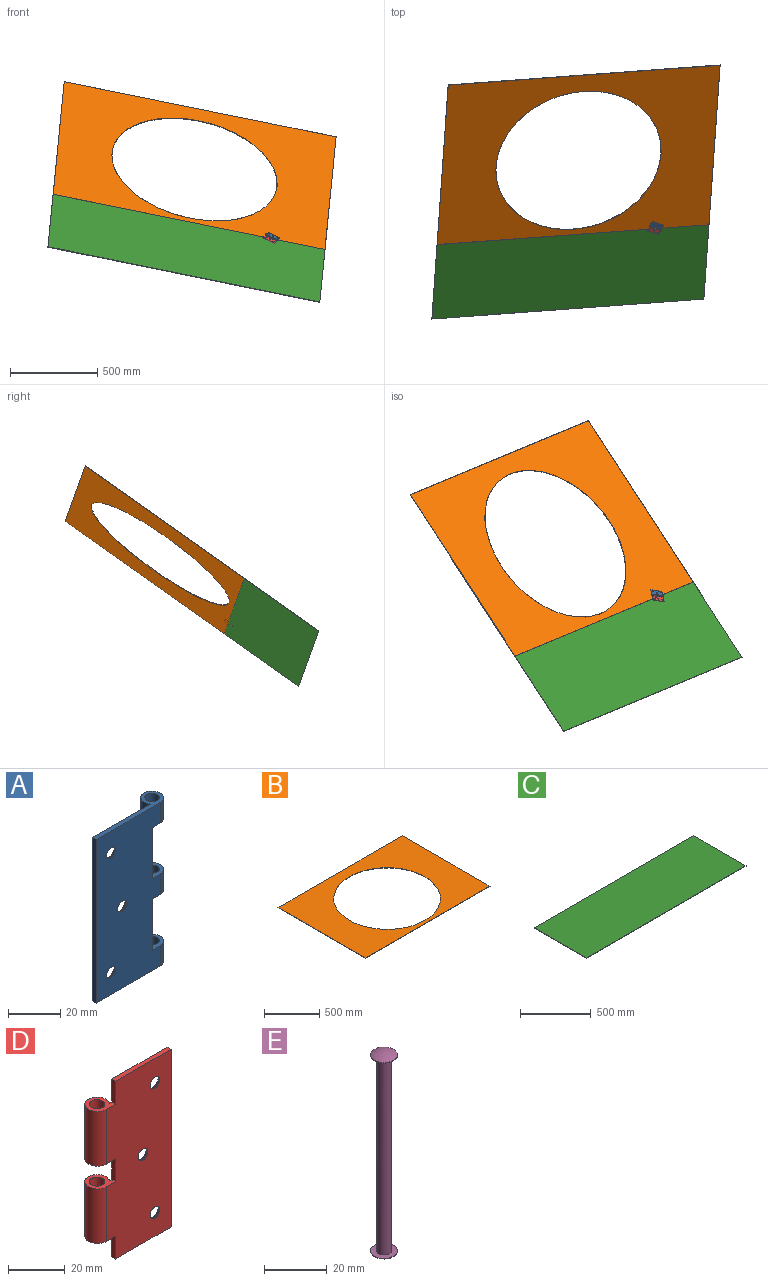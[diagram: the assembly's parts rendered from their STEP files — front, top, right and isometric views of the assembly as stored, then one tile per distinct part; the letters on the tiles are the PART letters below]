
ASSEMBLY  parts=5 mates=8
PART A: 26 faces, bbox 39.1x8.9x76.5 mm
  f0: cone r=2.41mm half-angle=40deg, axis (0,1,0), area 35.6mm2, adj f4,f20
  f1: cone r=2.41mm half-angle=40deg, axis (0,1,0), area 35.6mm2, adj f5,f20
  f2: cone r=2.41mm half-angle=40deg, axis (0,1,0), area 35.6mm2, adj f3,f20
  f3: cylinder r=2.41mm len=4.83mm, axis (0,1,0), area 7.1mm2, adj f2,f19
  f4: cylinder r=2.41mm len=4.83mm, axis (0,1,0), area 7.1mm2, adj f0,f19
  f5: cylinder r=2.41mm len=4.83mm, axis (0,1,0), area 7.1mm2, adj f1,f19
  f6: cylinder r=4.32mm len=9.53mm, axis (0,0,-1), area 184.9mm2, adj f12,f15,f20,f23
  f7: cylinder r=4.32mm len=9.53mm, axis (0,0,-1), area 184.9mm2, adj f13,f16,f20,f24
  f8: cylinder r=4.32mm len=9.53mm, axis (0,0,-1), area 184.9mm2, adj f14,f17,f20,f25
  f9: cylinder r=2.74mm len=9.53mm, axis (0,0,-1), area 164.2mm2, adj f14,f17
  f10: cylinder r=2.74mm len=9.53mm, axis (0,0,-1), area 164.2mm2, adj f12,f15
  f11: cylinder r=2.74mm len=9.53mm, axis (0,0,-1), area 164.2mm2, adj f13,f16
  f12: plane 39.12x8.89mm, normal (0,0,1), area 97.6mm2, adj f6,f10,f18,f19,f20,f23
  f13: plane 39.12x8.89mm, normal (0,0,-1), area 97.6mm2, adj f7,f11,f18,f19,f20,f24
  f14: plane 8.89x8.89mm, normal (0,0,1), area 40.1mm2, adj f8,f9,f19,f20,f21,f25
  f15: plane 8.89x8.89mm, normal (0,0,-1), area 40.1mm2, adj f6,f10,f19,f20,f21,f23
  f16: plane 8.89x8.89mm, normal (0,0,1), area 40.1mm2, adj f7,f11,f19,f20,f22,f24
  f17: plane 8.89x8.89mm, normal (0,0,-1), area 40.1mm2, adj f8,f9,f19,f20,f22,f25
  f18: plane 76.45x1.91mm, normal (-1,0,0), area 145.6mm2, adj f12,f13,f19,f20
  f19: plane 76.45x34.8mm, normal (0,-1,0), area 2386.7mm2, adj f3,f4,f5,f12,f13,f14,f15,f16
  f20: plane 76.45x31.4mm, normal (0,1,0), area 2221mm2, adj f0,f1,f2,f6,f7,f8,f12,f13
  f21: plane 23.94x1.91mm, normal (1,0,0), area 45.6mm2, adj f14,f15,f19,f20
  f22: plane 23.94x1.91mm, normal (1,0,0), area 45.6mm2, adj f16,f17,f19,f20
  f23: cylinder r=5.12mm len=9.53mm, axis (0,0,-1), area 37.1mm2, adj f6,f12,f15,f19
  f24: cylinder r=5.12mm len=9.53mm, axis (0,0,-1), area 37.1mm2, adj f7,f13,f16,f19
  f25: cylinder r=5.12mm len=9.53mm, axis (0,0,-1), area 37.1mm2, adj f8,f14,f17,f19
PART B: 7 faces, bbox 1590.7x1117.6x3.2 mm
  f0: plane 1117.6x3.18mm, normal (-1,0,0), area 3548.4mm2, adj f1,f3,f4,f5
  f1: plane 1590.68x3.18mm, normal (0,-1,0), area 5050.4mm2, adj f0,f2,f4,f5
  f2: plane 1117.6x3.18mm, normal (1,0,0), area 3548.4mm2, adj f1,f3,f4,f5
  f3: plane 1590.68x3.18mm, normal (0,1,0), area 5050.4mm2, adj f0,f2,f4,f5
  f4: plane 1590.68x1117.6mm, normal (0,0,-1), area 1046052.8mm2, adj f0,f1,f2,f3,f6
  f5: plane 1590.68x1117.6mm, normal (0,0,1), area 1046052.8mm2, adj f0,f1,f2,f3,f6
  f6: cylinder r=482.6mm len=965.2mm, axis (0,0,1), area 9627.4mm2, adj f4,f5
PART C: 6 faces, bbox 1590.7x520.7x3.2 mm
  f0: plane 1590.68x3.18mm, normal (0,1,0), area 5050.4mm2, adj f1,f3,f4,f5
  f1: plane 520.7x3.18mm, normal (-1,0,0), area 1653.2mm2, adj f0,f2,f4,f5
  f2: plane 1590.68x3.18mm, normal (0,-1,0), area 5050.4mm2, adj f1,f3,f4,f5
  f3: plane 520.7x3.18mm, normal (1,0,0), area 1653.2mm2, adj f0,f2,f4,f5
  f4: plane 1590.68x520.7mm, normal (0,0,-1), area 828264.5mm2, adj f0,f1,f2,f3
  f5: plane 1590.68x520.7mm, normal (0,0,1), area 828264.5mm2, adj f0,f1,f2,f3
PART D: 26 faces, bbox 36.6x8.9x76.5 mm
  f0: cone r=2.41mm half-angle=40deg, axis (0,1,0), area 35.6mm2, adj f1,f10
  f1: cylinder r=2.41mm len=4.83mm, axis (0,1,0), area 7.1mm2, adj f0,f19
  f2: cone r=2.41mm half-angle=40deg, axis (0,1,0), area 35.6mm2, adj f3,f10
  f3: cylinder r=2.41mm len=4.83mm, axis (0,1,0), area 7.1mm2, adj f2,f19
  f4: cone r=2.41mm half-angle=40deg, axis (0,1,0), area 35.6mm2, adj f5,f10
  f5: cylinder r=2.41mm len=4.83mm, axis (0,1,0), area 7.1mm2, adj f4,f19
  f6: cylinder r=4.32mm len=23.46mm, axis (0,0,-1), area 455.5mm2, adj f10,f13,f14,f25
  f7: cylinder r=4.32mm len=23.46mm, axis (0,0,-1), area 455.5mm2, adj f10,f15,f16,f24
  f8: cylinder r=2.74mm len=23.46mm, axis (0,0,1), area 404.4mm2, adj f13,f14
  f9: cylinder r=2.74mm len=23.46mm, axis (0,0,1), area 404.4mm2, adj f15,f16
  f10: plane 76.45x28.86mm, normal (0,1,0), area 2048.4mm2, adj f0,f2,f4,f6,f7,f13,f14,f15
  f11: cylinder r=4.57mm len=23.46mm, axis (0,0,1), area 99.5mm2, adj f15,f16,f19,f24
  f12: cylinder r=4.57mm len=23.46mm, axis (0,0,1), area 99.5mm2, adj f13,f14,f19,f25
  f13: plane 8.89x8.89mm, normal (0,0,1), area 40.8mm2, adj f6,f8,f10,f12,f19,f21,f25
  f14: plane 8.89x8.89mm, normal (0,0,-1), area 40.8mm2, adj f6,f8,f10,f12,f19,f22,f25
  f15: plane 8.89x8.89mm, normal (0,0,1), area 40.8mm2, adj f7,f9,f10,f11,f19,f22,f24
  f16: plane 8.89x8.89mm, normal (0,0,-1), area 40.8mm2, adj f7,f9,f10,f11,f19,f23,f24
  f17: plane 27.69x1.91mm, normal (0,0,-1), area 52.7mm2, adj f10,f19,f20,f23
  f18: plane 27.69x1.91mm, normal (0,0,1), area 52.7mm2, adj f10,f19,f20,f21
  f19: plane 76.45x32.26mm, normal (0,-1,0), area 2276.4mm2, adj f1,f3,f5,f11,f12,f13,f14,f15
  f20: plane 76.45x1.91mm, normal (1,0,0), area 145.6mm2, adj f10,f17,f18,f19
  f21: plane 9.84x1.91mm, normal (-1,0,0), area 18.7mm2, adj f10,f13,f18,f19
  f22: plane 9.84x1.91mm, normal (-1,0,0), area 18.7mm2, adj f10,f14,f15,f19
  f23: plane 9.84x1.91mm, normal (-1,0,0), area 18.7mm2, adj f10,f16,f17,f19
  f24: plane 23.46x0.32mm, normal (0,1,0), area 7.6mm2, adj f7,f11,f15,f16
  f25: plane 23.46x0.32mm, normal (0,1,0), area 7.6mm2, adj f6,f12,f13,f14
PART E: 7 faces, bbox 8.7x8.7x79.2 mm
  f0: cylinder r=4.32mm len=8.64mm, axis (0,0,1), area 5.4mm2, adj f1,f6
  f1: sphere r=8.86mm, area 62.5mm2, adj f0
  f2: cylinder r=2.38mm len=76.56mm, axis (0,0,1), area 1145.4mm2, adj f5,f6
  f3: sphere r=8.86mm, area 62.5mm2, adj f4
  f4: cylinder r=4.32mm len=8.64mm, axis (0,0,1), area 5.4mm2, adj f3,f5
  f5: plane 8.64x8.64mm, normal (0,0,1), area 40.8mm2, adj f2,f4
  f6: plane 8.64x8.64mm, normal (0,0,-1), area 40.8mm2, adj f0,f2
PLACE A rot(axis=(0.43,-0.36,-0.83),144deg) t=(348.51,-14.16,641.07)mm
PLACE B rot(axis=(0.94,0.33,0.01),37.5deg) t=(-232.79,555.79,402.2)mm
PLACE C rot(axis=(0.94,0.33,0.01),37.5deg) t=(-232.79,555.79,402.2)mm
PLACE D rot(axis=(0.43,-0.36,-0.83),144deg) t=(348.78,-14.25,640.93)mm
PLACE E rot(axis=(0.43,-0.36,-0.83),144deg) t=(348.56,-14.18,641.05)mm
MATE planar C.f3 <-> B.f2  axis (0.98,0.07,-0.2) through (641.6,-206.43,424.6)mm
MATE planar C.f5 <-> B.f5  axis (0.2,-0.57,0.79) through (-135.5,-264.62,583.69)mm
MATE slider E.f0 <-> D.f6  axis (-0.86,0.28,0.43) through (349.49,-16.8,644.67)mm
MATE planar C.f0 <-> B.f1  axis (0.06,0.82,0.58) through (-121,-51.44,732.44)mm
MATE planar A.f6 <-> D.f8  axis (-0.86,0.28,0.43) through (374.09,-24.94,632.47)mm
MATE planar E.f0 <-> A.f6  axis (0.86,-0.28,-0.43) through (316.61,-5.93,660.98)mm
MATE planar D.f19 <-> C.f5  axis (-0.2,0.57,-0.79) through (340.89,-27.15,633.61)mm
MATE slider A.f6 <-> D.f8  axis (0.86,-0.28,-0.43) through (345.35,-15.44,646.72)mm
